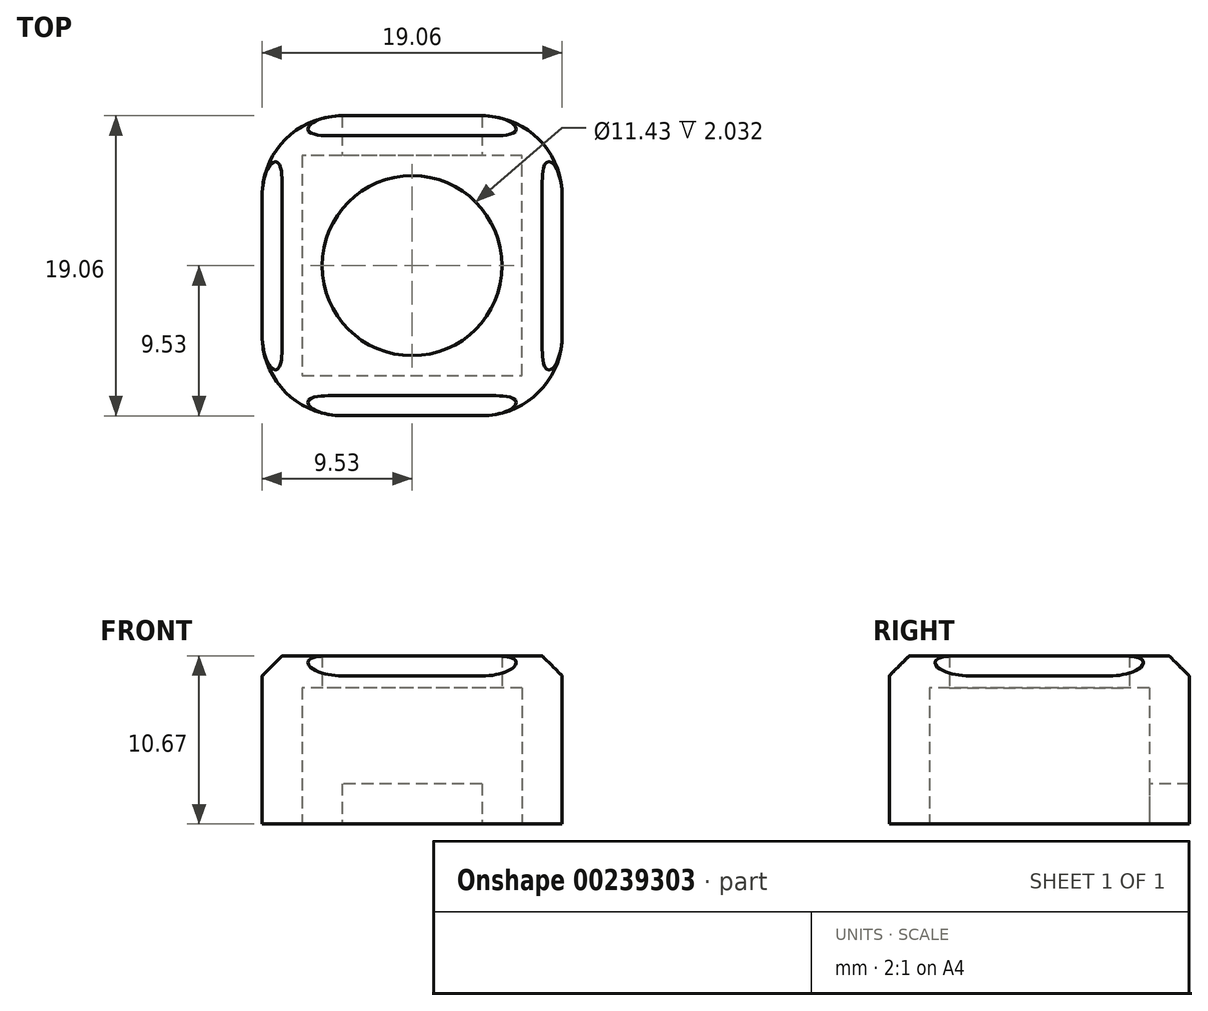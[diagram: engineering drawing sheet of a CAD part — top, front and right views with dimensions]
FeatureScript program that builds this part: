
annotation { "Feature Type Name" : "Feature", "Feature Type Description" : "" }
export const myFeature = defineFeature(function(context is Context, id is Id, definition is map)
    precondition{}
    {
        {
            var Q0;
            Q0=qCreatedBy(makeId("Top.planeOp"),FACE);
            var sketch = newSketch(context, id + "F0", { "sketchPlane" : qUnion([Q0])});
            skLineSegment(sketch, "E0.bottom", {"start": v(4.45, 9.53) * mm, "end": v(-4.44, 9.53) * mm});
            skLineSegment(sketch, "E0.top", {"start": v(4.44, -9.53) * mm, "end": v(-4.45, -9.53) * mm});
            skLineSegment(sketch, "E0.left", {"start": v(9.53, 4.44) * mm, "end": v(9.52, -4.45) * mm});
            skLineSegment(sketch, "E0.right", {"start": v(-9.52, 4.45) * mm, "end": v(-9.53, -4.44) * mm});
            skPoint(sketch, "E0.middle", {"position": v(0, 0) * mm});
            skPoint(sketch, "E1.visualSharp", {"position": v(9.53, 9.53) * mm});
            skArc(sketch, "E1.filletArc", {"start": v(9.53, 4.44) * mm, "mid": v(8.04, 8.04) * mm, "end": v(4.45, 9.52) * mm});
            skPoint(sketch, "E2.visualSharp", {"position": v(9.52, -9.53) * mm});
            skArc(sketch, "E2.filletArc", {"start": v(4.44, -9.53) * mm, "mid": v(8.04, -8.04) * mm, "end": v(9.52, -4.45) * mm});
            skPoint(sketch, "E3.visualSharp", {"position": v(-9.53, -9.53) * mm});
            skArc(sketch, "E3.filletArc", {"start": v(-9.53, -4.44) * mm, "mid": v(-8.04, -8.04) * mm, "end": v(-4.45, -9.53) * mm});
            skPoint(sketch, "E4.visualSharp", {"position": v(-9.52, 9.53) * mm});
            skArc(sketch, "E4.filletArc", {"start": v(-4.44, 9.53) * mm, "mid": v(-8.04, 8.04) * mm, "end": v(-9.52, 4.45) * mm});
            skLineSegment(sketch, "E5", {"start": v(-6.99, 4.44) * mm, "end": v(-6.99, -4.44) * mm});
            skLineSegment(sketch, "E6", {"start": v(-4.45, -6.99) * mm, "end": v(4.44, -6.98) * mm});
            skLineSegment(sketch, "E7", {"start": v(6.98, -4.44) * mm, "end": v(6.98, 4.44) * mm});
            skLineSegment(sketch, "E8", {"start": v(4.44, 6.99) * mm, "end": v(-4.45, 6.99) * mm});
            skLineSegment(sketch, "E9", {"start": v(-6.99, -4.44) * mm, "end": v(-6.99, -6.99) * mm});
            skLineSegment(sketch, "E10", {"start": v(-6.99, -6.99) * mm, "end": v(-4.45, -6.99) * mm});
            skLineSegment(sketch, "E11", {"start": v(4.44, -6.98) * mm, "end": v(6.98, -6.98) * mm});
            skLineSegment(sketch, "E12", {"start": v(6.98, -6.98) * mm, "end": v(6.98, -4.44) * mm});
            skLineSegment(sketch, "E13", {"start": v(6.98, 4.44) * mm, "end": v(6.98, 6.99) * mm});
            skLineSegment(sketch, "E14", {"start": v(6.98, 6.99) * mm, "end": v(4.44, 6.99) * mm});
            skLineSegment(sketch, "E15", {"start": v(-4.45, 6.99) * mm, "end": v(-6.99, 6.99) * mm});
            skLineSegment(sketch, "E16", {"start": v(-6.99, 6.99) * mm, "end": v(-6.99, 4.44) * mm});
            skSolve(sketch);
        }
        {
            var Q0;
            Q0 = qSketchRegion(id + "F0", true);
            extrude(context, id + "F1", {"entities" : qUnion([Q0]), "depth" : 8.64 * mm});
        }
        {
            var Q0;
            Q0=makeQuery(id+"F1.opExtrude","CAP_FACE",FACE,{"disambiguationData":[OSD([sQuery(id+"F0.wireOp",EDGE,"E0.bottom"),sQuery(id+"F0.wireOp",EDGE,"E0.top"),sQuery(id+"F0.wireOp",EDGE,"E0.left"),sQuery(id+"F0.wireOp",EDGE,"E0.right"),sQuery(id+"F0.wireOp",EDGE,"E1.filletArc"),sQuery(id+"F0.wireOp",EDGE,"E2.filletArc"),sQuery(id+"F0.wireOp",EDGE,"E3.filletArc"),sQuery(id+"F0.wireOp",EDGE,"E4.filletArc"),sQuery(id+"F0.wireOp",EDGE,"E5"),sQuery(id+"F0.wireOp",EDGE,"E6"),sQuery(id+"F0.wireOp",EDGE,"E7"),sQuery(id+"F0.wireOp",EDGE,"E8"),sQuery(id+"F0.wireOp",EDGE,"wgC2RLlI-Hau1-d7H5-G9N4-cS1JP17yu7oL"),sQuery(id+"F0.wireOp",EDGE,"lAkKgWFL-WTV1-v7QM-TzFQ-01UNfac3X1b8"),sQuery(id+"F0.wireOp",EDGE,"zw6CoFgg-ujwD-pftT-Hlzv-XdewnHxfykKs"),sQuery(id+"F0.wireOp",EDGE,"dNYyK7aG-stVS-WTjn-9Wlx-ELSWQ11dmL7K")])],"isStart":false});
            var sketch = newSketch(context, id + "F2", { "sketchPlane" : qUnion([Q0])});
            skLineSegment(sketch, "E17.bottom", {"start": v(4.45, 9.53) * mm, "end": v(-4.44, 9.53) * mm});
            skLineSegment(sketch, "E17.top", {"start": v(4.44, -9.52) * mm, "end": v(-4.45, -9.52) * mm});
            skLineSegment(sketch, "E17.left", {"start": v(9.53, 4.44) * mm, "end": v(9.52, -4.44) * mm});
            skLineSegment(sketch, "E17.right", {"start": v(-9.52, 4.45) * mm, "end": v(-9.53, -4.44) * mm});
            skPoint(sketch, "E17.middle", {"position": v(0, 0) * mm});
            skPoint(sketch, "E18.visualSharp", {"position": v(9.53, 9.53) * mm});
            skArc(sketch, "E18.filletArc", {"start": v(9.53, 4.44) * mm, "mid": v(8.04, 8.04) * mm, "end": v(4.45, 9.53) * mm});
            skPoint(sketch, "E19.visualSharp", {"position": v(-9.52, 9.53) * mm});
            skArc(sketch, "E19.filletArc", {"start": v(-4.45, 9.53) * mm, "mid": v(-8.04, 8.04) * mm, "end": v(-9.52, 4.45) * mm});
            skPoint(sketch, "E20.visualSharp", {"position": v(-9.53, -9.52) * mm});
            skArc(sketch, "E20.filletArc", {"start": v(-9.53, -4.44) * mm, "mid": v(-8.04, -8.04) * mm, "end": v(-4.45, -9.52) * mm});
            skPoint(sketch, "E21.visualSharp", {"position": v(9.52, -9.52) * mm});
            skArc(sketch, "E21.filletArc", {"start": v(4.44, -9.52) * mm, "mid": v(8.04, -8.04) * mm, "end": v(9.52, -4.44) * mm});
            skCircle(sketch, "E22", {"center": v(0, 0) * mm, "radius": 5.72 * mm});
            skSolve(sketch);
        }
        {
            var Q0;
            Q0 = qSketchRegion(id + "F2", true);
            extrude(context, id + "F3", {"entities" : qUnion([Q0]), "operationType" : NewBodyOperationType.ADD, "depth" : 2.03 * mm});
        }
        {
            var Q0;
            Q0=makeQuery(id+"F1.opExtrude","CAP_FACE",FACE,{"disambiguationData":[OSD([sQuery(id+"F0.wireOp",EDGE,"E0.bottom"),sQuery(id+"F0.wireOp",EDGE,"E0.top"),sQuery(id+"F0.wireOp",EDGE,"E0.left"),sQuery(id+"F0.wireOp",EDGE,"E0.right"),sQuery(id+"F0.wireOp",EDGE,"E1.filletArc"),sQuery(id+"F0.wireOp",EDGE,"E2.filletArc"),sQuery(id+"F0.wireOp",EDGE,"E3.filletArc"),sQuery(id+"F0.wireOp",EDGE,"E4.filletArc"),sQuery(id+"F0.wireOp",EDGE,"E5"),sQuery(id+"F0.wireOp",EDGE,"E6"),sQuery(id+"F0.wireOp",EDGE,"E7"),sQuery(id+"F0.wireOp",EDGE,"E8"),sQuery(id+"F0.wireOp",EDGE,"wgC2RLlI-Hau1-d7H5-G9N4-cS1JP17yu7oL"),sQuery(id+"F0.wireOp",EDGE,"lAkKgWFL-WTV1-v7QM-TzFQ-01UNfac3X1b8"),sQuery(id+"F0.wireOp",EDGE,"zw6CoFgg-ujwD-pftT-Hlzv-XdewnHxfykKs"),sQuery(id+"F0.wireOp",EDGE,"dNYyK7aG-stVS-WTjn-9Wlx-ELSWQ11dmL7K")])],"isStart":true});
            var sketch = newSketch(context, id + "F4", { "sketchPlane" : qUnion([Q0])});
            skLineSegment(sketch, "E23.bottom", {"start": v(-4.44, -9.53) * mm, "end": v(4.44, -9.53) * mm});
            skLineSegment(sketch, "E23.top", {"start": v(-4.44, -6.98) * mm, "end": v(4.44, -6.98) * mm});
            skLineSegment(sketch, "E23.left", {"start": v(-4.44, -9.53) * mm, "end": v(-4.44, -6.98) * mm});
            skLineSegment(sketch, "E23.right", {"start": v(4.44, -9.53) * mm, "end": v(4.44, -6.98) * mm});
            skSolve(sketch);
        }
        {
            var Q0;
            Q0 = qSketchRegion(id + "F4", true);
            extrude(context, id + "F5", {"entities" : qUnion([Q0]), "operationType" : NewBodyOperationType.REMOVE, "oppositeDirection" : true, "depth" : 2.54 * mm});
        }
        {
            var Q0;
            Q0=makeQuery(id+"F3.opExtrude","CAP_EDGE",EDGE,{"disambiguationData":[OSD([sQuery(id+"F2.wireOp",EDGE,"E17.right")])],"isStart":false});
            var Q1;
            Q1=makeQuery(id+"F3.opExtrude","CAP_EDGE",EDGE,{"disambiguationData":[OSD([sQuery(id+"F2.wireOp",EDGE,"E17.left")])],"isStart":false});
            var Q2;
            Q2=makeQuery(id+"F3.opExtrude","CAP_EDGE",EDGE,{"disambiguationData":[OSD([sQuery(id+"F2.wireOp",EDGE,"E17.top")])],"isStart":false});
            var Q3;
            Q3=makeQuery(id+"F3.opExtrude","CAP_EDGE",EDGE,{"disambiguationData":[OSD([sQuery(id+"F2.wireOp",EDGE,"E17.bottom")])],"isStart":false});
            chamfer(context, id + "F6", {"entities" : qUnion([Q0, Q1, Q2, Q3]), "width" : 1.27 * mm});
        }
        {
            var Q0;
            Q0=makeQuery(id+"F3.opExtrude","CAP_EDGE",EDGE,{"disambiguationData":[OSD([sQuery(id+"F2.wireOp",EDGE,"E18.filletArc")])],"isStart":false});
            var Q1;
            Q1=makeQuery(id+"F3.opExtrude","CAP_EDGE",EDGE,{"disambiguationData":[OSD([sQuery(id+"F2.wireOp",EDGE,"E20.filletArc")])],"isStart":false});
            var Q2;
            Q2=makeQuery(id+"F3.opExtrude","CAP_EDGE",EDGE,{"disambiguationData":[OSD([sQuery(id+"F2.wireOp",EDGE,"E19.filletArc")])],"isStart":false});
            var Q3;
            Q3=makeQuery(id+"F3.opExtrude","CAP_EDGE",EDGE,{"disambiguationData":[OSD([sQuery(id+"F2.wireOp",EDGE,"E21.filletArc")])],"isStart":false});
            fillet(context, id + "F7", {"entities" : qUnion([Q0, Q1, Q2, Q3]), "radius" : 1.27 * mm, "tangentPropagation" : true, "allowEdgeOverflow" : false});
        }
    });
